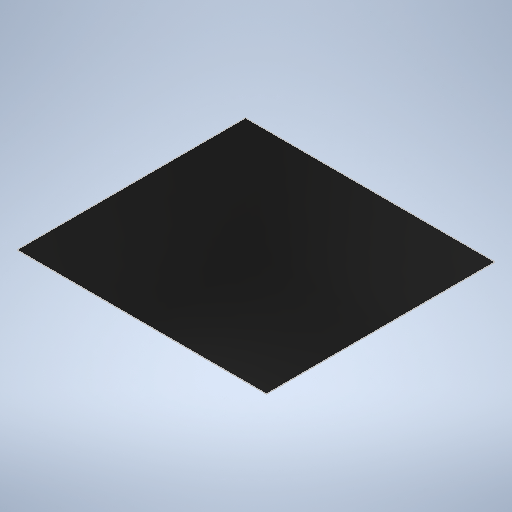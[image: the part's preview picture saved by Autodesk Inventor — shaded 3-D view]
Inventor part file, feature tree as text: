
AUTODESK INVENTOR PART (.ipt)
format: ipt  version: 2025 (Build 290162000, 162)  size: 209,920 bytes
history: native  units: in
note: dims shown in document units (in); Inventor stores cm internally (conversion verified against a paired STEP export)
features: extrude x1
ambient origin geometry x8: Origin, YZ Plane, XZ Plane, XY Plane, X Axis, Y Axis, Z Axis, Center Point
bodies: Solid1 (feature_tree)
feature tree (1):
  extrude  "Extrusion1"  Depth=1.7165in
